# Revit family: Side_Folding_Door_9100-CHI-EL_Prestige
name_source: partatom
category: Specialty Equipment
units: mm (PartAtom-declared; Revit-internal decimal feet)

## family parameters
Always vertical = Yes
Cut with Voids When Loaded = No
Enable Cutting in Views = No
Maintain Annotation Orientation = No
OmniClass Number = 23.30.10.21
OmniClass Title = Special Function Doors
Part Type = Normal
Room Calculation Point = No
Round Connector Dimension = Use Diameter
Shared = No
Work Plane-Based = No

## types (1)
- EL - Prestige
    Assembly Code = B2030420
    C Bottom Offset = 0' - 0 3/4"
    C Max Height = 14' - 0"
    C Max Width = 25' - 0"
    C Min Height = 4' - 0"
    C Min Width = 2' - 3 1/2"
    C Panel Width = 0' - 7"
    C Pocket Width = 0' - 8"
    C Top Gap = 0' - 1 1/2"
    C Track Height = 0' - 1 5/8"
    C Track Thickness = 0' - 0 1/8"
    C Track Width = 0' - 1 3/8"
    Constraints = 1
    Counter = Yes
    Default Elevation = 0' - 0"
    Description = Side-Folding Grille
    Floor = No
    Frame = Metal - Powder Coat - C.H.I Overhead Doors - White
    Glass = Glass - C.H.I Overhead Doors - Frosted
    Keynote = 08330
    Manufacturer = C.H.I. Overhead Doors
    Manufacturer Fax Number = 800-677-2650
    Model = EL - Prestige
    Product Documentation Link = Contact Manufacturer for More Information
    Product Page URL = Contact Manufacturer for More Information
    URL = https://www.chiohd.com
    Version = 2021-v1.a

## geometry (parser evidence)
native form markers: Sweep x14
no freeform markers — native parametric forms only
